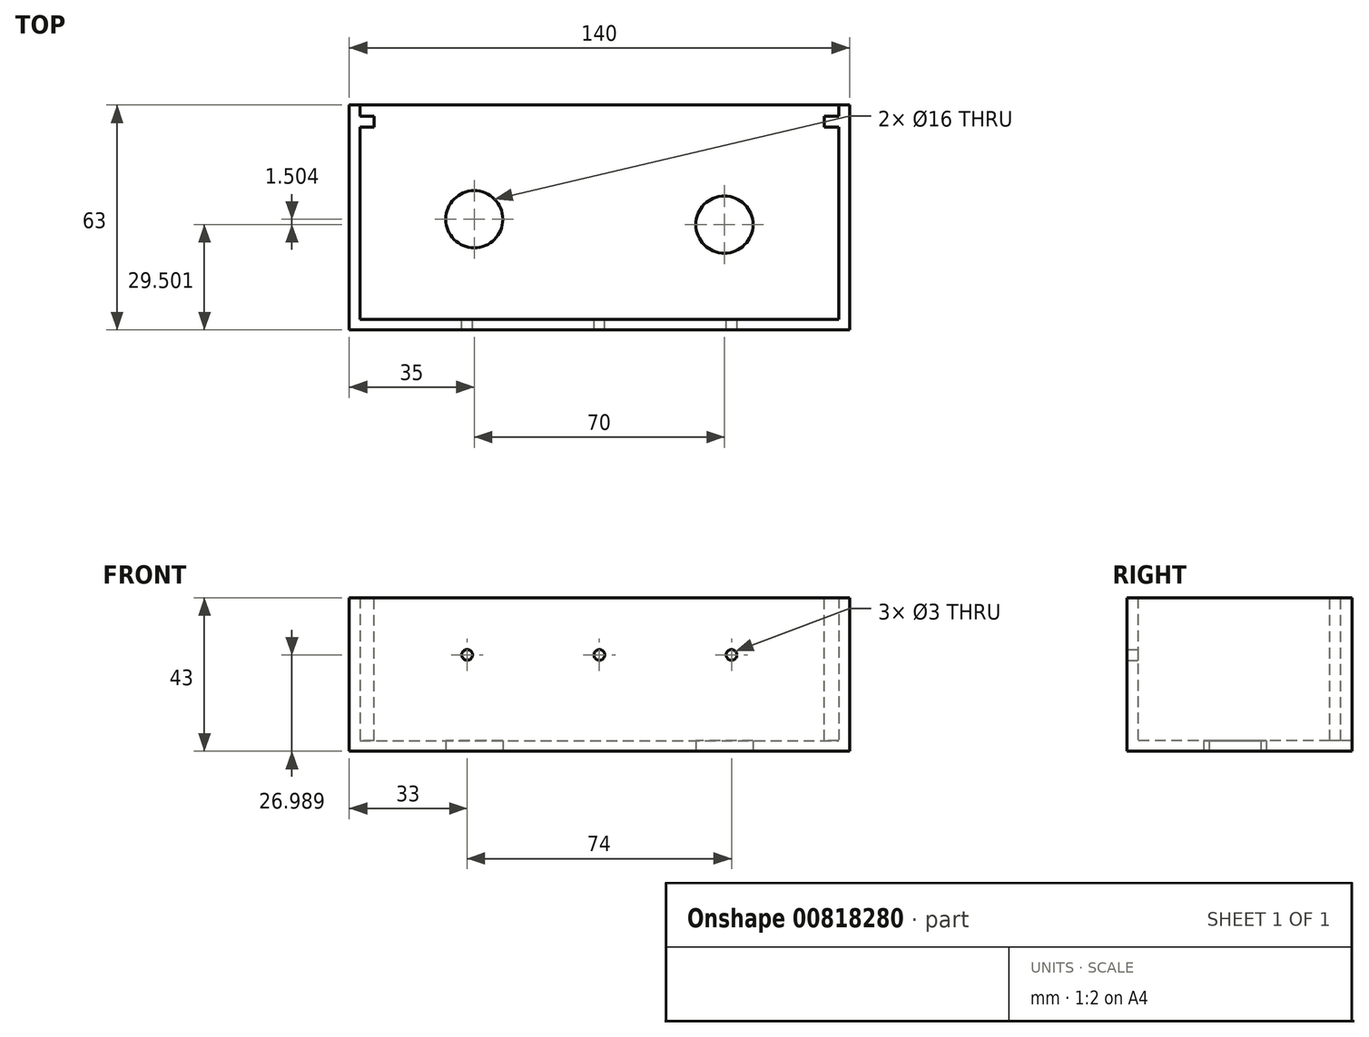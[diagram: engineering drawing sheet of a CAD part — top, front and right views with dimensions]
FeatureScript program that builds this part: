
annotation { "Feature Type Name" : "Feature", "Feature Type Description" : "" }
export const myFeature = defineFeature(function(context is Context, id is Id, definition is map)
    precondition{}
    {
        {
            var Q0;
            Q0=qCreatedBy(makeId("Top.planeOp"),FACE);
            var sketch = newSketch(context, id + "F0", { "sketchPlane" : qUnion([Q0])});
            skLineSegment(sketch, "E0.bottom", {"start": v(-80, 33.03) * mm, "end": v(60, 33.03) * mm});
            skLineSegment(sketch, "E0.top", {"start": v(-80, -32.97) * mm, "end": v(60, -32.97) * mm});
            skLineSegment(sketch, "E0.left", {"start": v(-80, 33.03) * mm, "end": v(-80, -32.97) * mm});
            skLineSegment(sketch, "E0.right", {"start": v(60, 33.03) * mm, "end": v(60, -32.97) * mm});
            skLineSegment(sketch, "E1.left", {"start": v(-80, -32.97) * mm, "end": v(-80, 0.03) * mm});
            skLineSegment(sketch, "E1.right", {"start": v(60, -9.97) * mm, "end": v(60, 0.03) * mm});
            skLineSegment(sketch, "E2.bottom", {"start": v(-80, -32.97) * mm, "end": v(-45, -32.97) * mm});
            skLineSegment(sketch, "E2.top", {"start": v(-80, 33.03) * mm, "end": v(-60, 33.03) * mm});
            skLineSegment(sketch, "E2.left", {"start": v(-80, -32.97) * mm, "end": v(-80, 33.03) * mm});
            skLineSegment(sketch, "E3.bottom", {"start": v(-45, -32.97) * mm, "end": v(-25, -32.97) * mm});
            skLineSegment(sketch, "E3.top", {"start": v(-60, 33.03) * mm, "end": v(-40, 33.03) * mm});
            skLineSegment(sketch, "E4.bottom", {"start": v(-25, -32.97) * mm, "end": v(-5, -32.97) * mm});
            skLineSegment(sketch, "E4.top", {"start": v(-40, 33.03) * mm, "end": v(-20, 33.03) * mm});
            skPoint(sketch, "E5.oppositeSnap0", {"position": v(-10, 33.03) * mm});
            skLineSegment(sketch, "E5.bottom", {"start": v(-5, -32.97) * mm, "end": v(15, -32.97) * mm});
            skLineSegment(sketch, "E5.top", {"start": v(-20, 33.03) * mm, "end": v(0, 33.03) * mm});
            skLineSegment(sketch, "E6.bottom", {"start": v(15, -32.97) * mm, "end": v(35, -32.97) * mm});
            skLineSegment(sketch, "E6.top", {"start": v(0, 33.03) * mm, "end": v(20, 33.03) * mm});
            skLineSegment(sketch, "E7.bottom", {"start": v(35, -32.97) * mm, "end": v(55, -32.97) * mm});
            skLineSegment(sketch, "E7.top", {"start": v(20, 33.03) * mm, "end": v(40, 33.03) * mm});
            skLineSegment(sketch, "E8.left", {"start": v(-80, -32.97) * mm, "end": v(-80, -2.97) * mm});
            skLineSegment(sketch, "E8.right", {"start": v(60, -24.97) * mm, "end": v(60, -4.97) * mm});
            skLineSegment(sketch, "E9.left", {"start": v(-80, 33.03) * mm, "end": v(-80, 18.03) * mm});
            skLineSegment(sketch, "E9.right", {"start": v(60, 33.03) * mm, "end": v(60, 18.03) * mm});
            skCircle(sketch, "E10", {"center": v(-45, 1.03) * mm, "radius": 8 * mm});
            skCircle(sketch, "E11", {"center": v(25, -0.47) * mm, "radius": 8 * mm});
            skLineSegment(sketch, "E12.left", {"start": v(-80, -32.97) * mm, "end": v(-80, -17.97) * mm});
            skLineSegment(sketch, "E12.right", {"start": v(60, -32.97) * mm, "end": v(60, -14.97) * mm});
            skLineSegment(sketch, "E13.top", {"start": v(-80, -29.97) * mm, "end": v(60, -29.97) * mm});
            skLineSegment(sketch, "E13.left", {"start": v(-80, -32.97) * mm, "end": v(-80, -29.97) * mm});
            skLineSegment(sketch, "E13.right", {"start": v(60, -32.97) * mm, "end": v(60, -29.97) * mm});
            skSolve(sketch);
        }
        {
            var Q0;
            Q0=makeQuery(id+"F0.imprint","IMPRINT",FACE,{"disambiguationData":[TD([[makeQuery(id+"F0.imprint","IMPRINT",EDGE,{"derivedFrom":sQuery(id+"F0.wireOp",EDGE,"E0.right")}),-1.0]])]});
            extrude(context, id + "F1", {"entities" : qUnion([Q0]), "depth" : 3 * mm, "offsetDistance" : 25 * mm});
        }
        {
            var Q0;
            Q0=makeQuery(id+"F1.opExtrude","CAP_FACE",FACE,{"disambiguationData":[OSD([sQuery(id+"F0.wireOp",EDGE,"E0.right"),sQuery(id+"F0.wireOp",EDGE,"E1.right"),sQuery(id+"F0.wireOp",EDGE,"E2.left"),sQuery(id+"F0.wireOp",EDGE,"E8.left"),sQuery(id+"F0.wireOp",EDGE,"E8.right"),sQuery(id+"F0.wireOp",EDGE,"E0.bottom"),sQuery(id+"F0.wireOp",EDGE,"E9.left"),sQuery(id+"F0.wireOp",EDGE,"E9.right"),sQuery(id+"F0.wireOp",EDGE,"l78r6zbi-zdNL-ogfi-jeJ1-84AOC1EXPDmI"),sQuery(id+"F0.wireOp",EDGE,"7xFXzIXv-dOzj-SHI9-m5NP-5MGqcVb28G0k"),sQuery(id+"F0.wireOp",EDGE,"E10"),sQuery(id+"F0.wireOp",EDGE,"k8Uu2vQ0-tXef-bBox-vRSx-lKBiwxJhI1xb"),sQuery(id+"F0.wireOp",EDGE,"E11"),sQuery(id+"F0.wireOp",EDGE,"5OqNOj1d-C8S8-WuIc-Ppvz-3VOTpNMQOR2k"),sQuery(id+"F0.wireOp",EDGE,"E12.left"),sQuery(id+"F0.wireOp",EDGE,"E12.right"),sQuery(id+"F0.wireOp",EDGE,"HoM0chx2-d7kJ-X9MT-WdqG-gqhH9dmnozYe"),sQuery(id+"F0.wireOp",EDGE,"JgkcrWLJ-2lYI-B5tP-8zwM-9y0SQbQCKJUD"),sQuery(id+"F0.wireOp",EDGE,"uQcqgJcq-6ofs-f9DD-1k3D-WOd607GN4n9v"),sQuery(id+"F0.wireOp",EDGE,"E13.top")])],"isStart":false});
            var sketch = newSketch(context, id + "F2", { "sketchPlane" : qUnion([Q0])});
            skLineSegment(sketch, "E14.bottom", {"start": v(-80, -29.97) * mm, "end": v(60, -29.97) * mm});
            skLineSegment(sketch, "E14.top", {"start": v(-80, -26.97) * mm, "end": v(60, -26.97) * mm});
            skLineSegment(sketch, "E14.left", {"start": v(-80, -29.97) * mm, "end": v(-80, -26.97) * mm});
            skLineSegment(sketch, "E14.right", {"start": v(60, -29.97) * mm, "end": v(60, -26.97) * mm});
            skLineSegment(sketch, "E15.left", {"start": v(-80, 33.03) * mm, "end": v(-80, 30.03) * mm});
            skLineSegment(sketch, "E15.right", {"start": v(60, 33.03) * mm, "end": v(60, 30.03) * mm});
            skLineSegment(sketch, "E16.bottom", {"start": v(-80, 33.03) * mm, "end": v(-77, 33.03) * mm});
            skLineSegment(sketch, "E16.top", {"start": v(-80, -29.97) * mm, "end": v(-77, -29.97) * mm});
            skLineSegment(sketch, "E16.left", {"start": v(-80, 33.03) * mm, "end": v(-80, -29.97) * mm});
            skLineSegment(sketch, "E16.right", {"start": v(-77, 33.03) * mm, "end": v(-77, -29.97) * mm});
            skLineSegment(sketch, "E17.bottom", {"start": v(60, 33.03) * mm, "end": v(57, 33.03) * mm});
            skLineSegment(sketch, "E17.top", {"start": v(60, -29.97) * mm, "end": v(57, -29.97) * mm});
            skLineSegment(sketch, "E17.left", {"start": v(60, 33.03) * mm, "end": v(60, -29.97) * mm});
            skLineSegment(sketch, "E17.right", {"start": v(57, 33.03) * mm, "end": v(57, -29.97) * mm});
            skSolve(sketch);
        }
        {
            var Q0;
            Q0=qSketchRegion(id+"F2",true);
            extrude(context, id + "F3", {"entities" : qUnion([Q0]), "operationType" : NewBodyOperationType.ADD, "depth" : 40 * mm, "offsetDistance" : 25 * mm});
        }
        {
            var Q0;
            Q0=makeQuery(id+"F3.opExtrude","SWEPT_FACE",FACE,{"disambiguationData":[OSD([sQuery(id+"F2.wireOp",EDGE,"E16.right")])]});
            var sketch = newSketch(context, id + "F4", { "sketchPlane" : qUnion([Q0])});
            skLineSegment(sketch, "E18.bottom", {"start": v(33.03, 43) * mm, "end": v(29.83, 43) * mm});
            skLineSegment(sketch, "E18.top", {"start": v(33.03, 3) * mm, "end": v(29.83, 3) * mm});
            skLineSegment(sketch, "E18.left", {"start": v(33.03, 43) * mm, "end": v(33.03, 3) * mm});
            skLineSegment(sketch, "E18.right", {"start": v(29.83, 43) * mm, "end": v(29.83, 3) * mm});
            skLineSegment(sketch, "E19.bottom", {"start": v(29.83, 43) * mm, "end": v(26.83, 43) * mm});
            skLineSegment(sketch, "E19.top", {"start": v(29.83, 3) * mm, "end": v(26.83, 3) * mm});
            skLineSegment(sketch, "E19.right", {"start": v(26.83, 43) * mm, "end": v(26.83, 3) * mm});
            skSolve(sketch);
        }
        {
            var Q0;
            Q0=makeQuery(id+"F4.imprint","IMPRINT",FACE,{"disambiguationData":[TD([[makeQuery(id+"F4.imprint","IMPRINT",EDGE,{"derivedFrom":sQuery(id+"F4.wireOp",EDGE,"E19.bottom")}),1.0]])]});
            extrude(context, id + "F5", {"entities" : qUnion([Q0]), "operationType" : NewBodyOperationType.ADD, "depth" : 134 * mm, "offsetDistance" : 25 * mm});
        }
        {
            var Q0;
            Q0=makeQuery(id+"F5.boolean.opBoolean","MERGE",FACE,{"derivedFrom":[makeQuery(id+"F3.opExtrude","CAP_FACE",FACE,{"disambiguationData":[OSD([sQuery(id+"F2.wireOp",EDGE,"E14.bottom"),sQuery(id+"F2.wireOp",EDGE,"E14.top"),sQuery(id+"F2.wireOp",EDGE,"E16.bottom"),sQuery(id+"F2.wireOp",EDGE,"E16.top"),sQuery(id+"F2.wireOp",EDGE,"E16.left"),sQuery(id+"F2.wireOp",EDGE,"E16.right"),sQuery(id+"F2.wireOp",EDGE,"E17.bottom"),sQuery(id+"F2.wireOp",EDGE,"E17.top"),sQuery(id+"F2.wireOp",EDGE,"E17.left"),sQuery(id+"F2.wireOp",EDGE,"E17.right")])],"isStart":false}),makeQuery(id+"F5.opExtrude","SWEPT_FACE",FACE,{"disambiguationData":[OSD([sQuery(id+"F4.wireOp",EDGE,"E19.bottom")])]})]});
            var sketch = newSketch(context, id + "F6", { "sketchPlane" : qUnion([Q0])});
            skLineSegment(sketch, "E20.bottom", {"start": v(-73, 29.83) * mm, "end": v(53, 29.83) * mm});
            skLineSegment(sketch, "E20.top", {"start": v(-73, 26.83) * mm, "end": v(53, 26.83) * mm});
            skLineSegment(sketch, "E20.left", {"start": v(-73, 29.83) * mm, "end": v(-73, 26.83) * mm});
            skLineSegment(sketch, "E20.right", {"start": v(53, 29.83) * mm, "end": v(53, 26.83) * mm});
            skSolve(sketch);
        }
        {
            var Q0;
            Q0=qSketchRegion(id+"F6",true);
            extrude(context, id + "F7", {"entities" : qUnion([Q0]), "operationType" : NewBodyOperationType.REMOVE, "oppositeDirection" : true, "depth" : 40 * mm, "offsetDistance" : 25 * mm});
        }
        {
            var Q0;
            Q0=makeQuery(id+"F3.opExtrude","SWEPT_FACE",FACE,{"disambiguationData":[OSD([sQuery(id+"F2.wireOp",EDGE,"E14.top")])]});
            var sketch = newSketch(context, id + "F8", { "sketchPlane" : qUnion([Q0])});
            skLineSegment(sketch, "E21.bottom", {"start": v(77, 43) * mm, "end": v(-57, 43) * mm});
            skLineSegment(sketch, "E21.left", {"start": v(77, 43) * mm, "end": v(77, 26.99) * mm});
            skLineSegment(sketch, "E21.right", {"start": v(-57, 43) * mm, "end": v(-57, 26.99) * mm});
            skCircle(sketch, "E22", {"center": v(47, 26.99) * mm, "radius": 1.5 * mm});
            skCircle(sketch, "E23", {"center": v(-27, 26.99) * mm, "radius": 1.5 * mm});
            skCircle(sketch, "E24", {"center": v(10, 26.99) * mm, "radius": 1.5 * mm});
            skSolve(sketch);
        }
        {
            var Q0;
            Q0=makeQuery(id+"F8.imprint","IMPRINT",FACE,{"disambiguationData":[TD([[makeQuery(id+"F8.imprint","IMPRINT",EDGE,{"derivedFrom":sQuery(id+"F8.wireOp",EDGE,"E22")}),1.0]])]});
            var Q1;
            Q1=makeQuery(id+"F8.imprint","IMPRINT",FACE,{"disambiguationData":[TD([[makeQuery(id+"F8.imprint","IMPRINT",EDGE,{"derivedFrom":sQuery(id+"F8.wireOp",EDGE,"E23")}),1.0]])]});
            var Q2;
            Q2=makeQuery(id+"F8.imprint","IMPRINT",FACE,{"disambiguationData":[TD([[makeQuery(id+"F8.imprint","IMPRINT",EDGE,{"derivedFrom":sQuery(id+"F8.wireOp",EDGE,"E24")}),1.0]])]});
            extrude(context, id + "F9", {"entities" : qUnion([Q0, Q1, Q2]), "operationType" : NewBodyOperationType.REMOVE, "oppositeDirection" : true, "depth" : 3 * mm, "offsetDistance" : 25 * mm});
        }
    });
